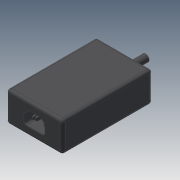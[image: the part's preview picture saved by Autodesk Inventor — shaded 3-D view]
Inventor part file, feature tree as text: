
AUTODESK INVENTOR PART (.ipt)
format: ipt  version: 2020.3 (Build 243373000, 373)  size: 492,544 bytes
history: native  units: in
note: dims shown in document units (in); Inventor stores cm internally (conversion verified against a paired STEP export)
features: imported_body x4, extrude x3, sketch x3, fillet x2, projected_geometry x2
ambient origin geometry x8: Origin, YZ Plane, XZ Plane, XY Plane, X Axis, Y Axis, Z Axis, Center Point
bodies: Solid1 (feature_tree), Solid2 (feature_tree), Solid3 (feature_tree), Solid4 (feature_tree)
feature tree (14):
  extrude  "Extrusion1"  Depth=2.6378in
  extrude  "Extrusion2"  Depth=1.0in TaperAngle=0.0deg
  fillet  "Fillet1"  Radius=0.125in
  fillet  "Fillet2"  Radius=0.125in
  extrude  "Extrusion3"  [1 undecoded]
  sketch  "Sketch1"  dims[d0=2.6378in d1=1.4173in]
  projected_geometry  "Projected Loop1"
  sketch  "Sketch2"  dims[d2=4.2323in d3=0.0in d4=1.0in d5=0.0in d6=0.125in d7=0.125in]
  projected_geometry  "Projected Loop2"
  sketch  "Sketch3"  dims[d8=1.0in d9=0.0in]
  imported_body  "Imported1"
  imported_body  "Imported2"
  imported_body  "Imported3"
  imported_body  "Imported4"
note: 1 required parameter value undecoded (feature->parameter linkage not recoverable at this tier; creation-order binding heuristic only, values carry confidence <= 0.55)
